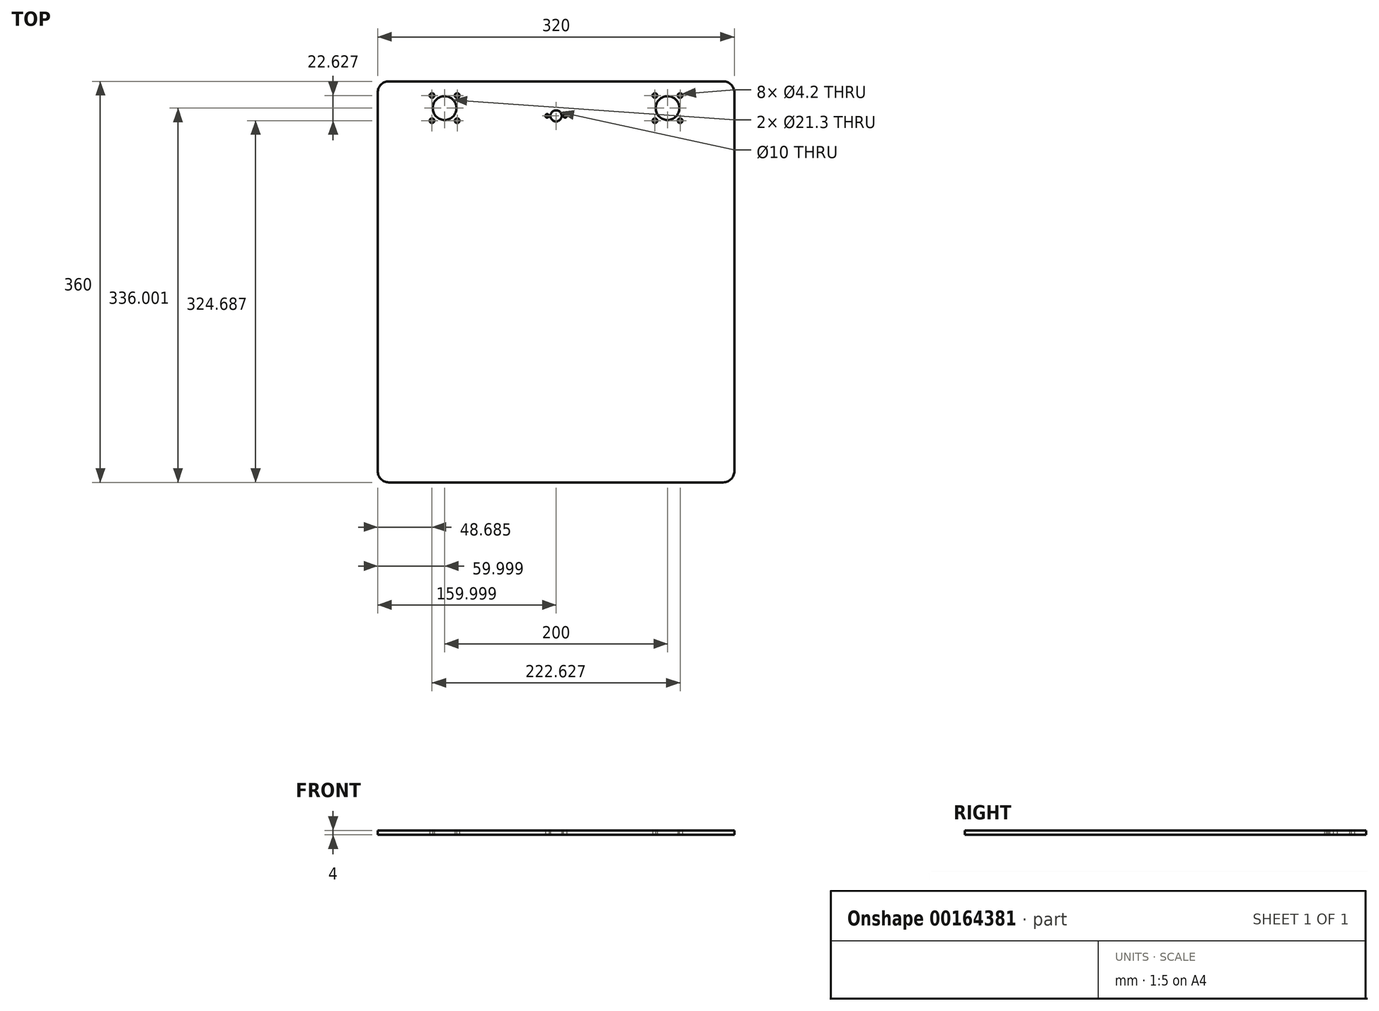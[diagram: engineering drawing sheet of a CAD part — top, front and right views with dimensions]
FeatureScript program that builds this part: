
annotation { "Feature Type Name" : "Feature", "Feature Type Description" : "" }
export const myFeature = defineFeature(function(context is Context, id is Id, definition is map)
    precondition{}
    {
        {
            var Q0;
            Q0=qCreatedBy(makeId("Top.planeOp"),FACE);
            var sketch = newSketch(context, id + "F0", { "sketchPlane" : qUnion([Q0])});
            skLineSegment(sketch, "E0.bottom", {"start": v(-144, 157.92) * mm, "end": v(156, 157.92) * mm});
            skLineSegment(sketch, "E0.top", {"start": v(-144, -202.08) * mm, "end": v(156, -202.08) * mm});
            skLineSegment(sketch, "E0.left", {"start": v(-154, 147.92) * mm, "end": v(-154, -192.08) * mm});
            skLineSegment(sketch, "E0.right", {"start": v(166, 147.92) * mm, "end": v(166, -192.08) * mm});
            skLineSegment(sketch, "E1", {"start": v(6, 157.92) * mm, "end": v(6, -202.08) * mm, "construction": true});
            skCircle(sketch, "E2", {"center": v(-94, 133.92) * mm, "radius": 10.65 * mm});
            skCircle(sketch, "E3", {"center": v(106, 133.92) * mm, "radius": 10.65 * mm});
            skCircle(sketch, "E4", {"center": v(6, 126.92) * mm, "radius": 5 * mm});
            skCircle(sketch, "E5", {"center": v(106, 133.92) * mm, "radius": 16 * mm, "construction": true});
            skCircle(sketch, "E6", {"center": v(94.69, 145.23) * mm, "radius": 2.1 * mm});
            skCircle(sketch, "E7", {"center": v(117.31, 145.23) * mm, "radius": 2.1 * mm});
            skCircle(sketch, "E8", {"center": v(117.31, 122.6) * mm, "radius": 2.1 * mm});
            skCircle(sketch, "E9", {"center": v(94.69, 122.6) * mm, "radius": 2.1 * mm});
            skLineSegment(sketch, "E10", {"start": v(106, 133.92) * mm, "end": v(106, 149.92) * mm, "construction": true});
            skLineSegment(sketch, "E11", {"start": v(106, 133.92) * mm, "end": v(94.69, 145.23) * mm, "construction": true});
            skCircle(sketch, "E12", {"center": v(-94, 133.92) * mm, "radius": 16 * mm, "construction": true});
            skCircle(sketch, "E13", {"center": v(-105.31, 145.23) * mm, "radius": 2.1 * mm});
            skCircle(sketch, "E14", {"center": v(-82.69, 145.23) * mm, "radius": 2.1 * mm});
            skCircle(sketch, "E15", {"center": v(-82.69, 122.6) * mm, "radius": 2.1 * mm});
            skCircle(sketch, "E16", {"center": v(-105.31, 122.6) * mm, "radius": 2.1 * mm});
            skLineSegment(sketch, "E17", {"start": v(-94, 133.92) * mm, "end": v(-94, 149.92) * mm, "construction": true});
            skLineSegment(sketch, "E18", {"start": v(-94, 133.92) * mm, "end": v(-105.31, 145.23) * mm, "construction": true});
            skLineSegment(sketch, "E19", {"start": v(-2.7, 126.92) * mm, "end": v(14.9, 126.92) * mm, "construction": true});
            skCircle(sketch, "E20", {"center": v(14, 126.92) * mm, "radius": 1.6 * mm});
            skCircle(sketch, "E21", {"center": v(-2, 126.92) * mm, "radius": 1.6 * mm});
            skPoint(sketch, "E22.visualSharp", {"position": v(-154, 157.92) * mm});
            skArc(sketch, "E22.filletArc", {"start": v(-144, 157.92) * mm, "mid": v(-151.07, 155) * mm, "end": v(-154, 147.92) * mm});
            skPoint(sketch, "E23.visualSharp", {"position": v(166, 157.92) * mm});
            skArc(sketch, "E23.filletArc", {"start": v(166, 147.92) * mm, "mid": v(163.07, 155) * mm, "end": v(156, 157.92) * mm});
            skPoint(sketch, "E24.visualSharp", {"position": v(166, -202.08) * mm});
            skArc(sketch, "E24.filletArc", {"start": v(156, -202.08) * mm, "mid": v(163.07, -199.15) * mm, "end": v(166, -192.08) * mm});
            skPoint(sketch, "E25.visualSharp", {"position": v(-154, -202.08) * mm});
            skArc(sketch, "E25.filletArc", {"start": v(-154, -192.08) * mm, "mid": v(-151.07, -199.15) * mm, "end": v(-144, -202.08) * mm});
            skSolve(sketch);
        }
        {
            var Q0;
            Q0 = qSketchRegion(id + "F0", true);
            extrude(context, id + "F1", {"entities" : qUnion([Q0]), "depth" : 4 * mm});
        }
    });
